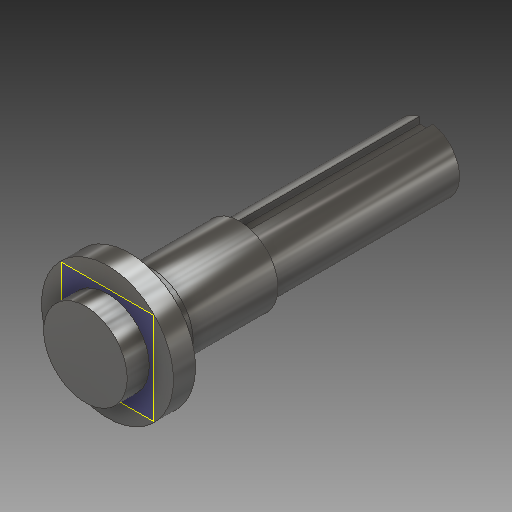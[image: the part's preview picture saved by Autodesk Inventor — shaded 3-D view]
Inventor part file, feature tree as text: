
AUTODESK INVENTOR PART (.ipt)
format: ipt  version: 2019 (Build 230136000, 136)  size: 156,672 bytes
history: native  units: in
note: dims shown in document units (in); Inventor stores cm internally (conversion verified against a paired STEP export)
features: sketch x5, other x3, plane x1
ambient origin geometry x8: Origin, YZ Plane, XZ Plane, XY Plane, X Axis, Y Axis, Z Axis, Center Point
bodies: Solid1 (feature_tree)
feature tree (9):
  other  "project handle part(1)_CPY.ipt"
  other  "Solid1::project handle part(1)_CPY.ipt"
  other  "TaggingFeature1"
  sketch  "Sketch1"  dims[d0=0.3937in]
  sketch  "Sketch2"
  sketch  "Sketch3"
  sketch  "Sketch4"
  sketch  "Sketch5"
  plane  "Work Plane1"
